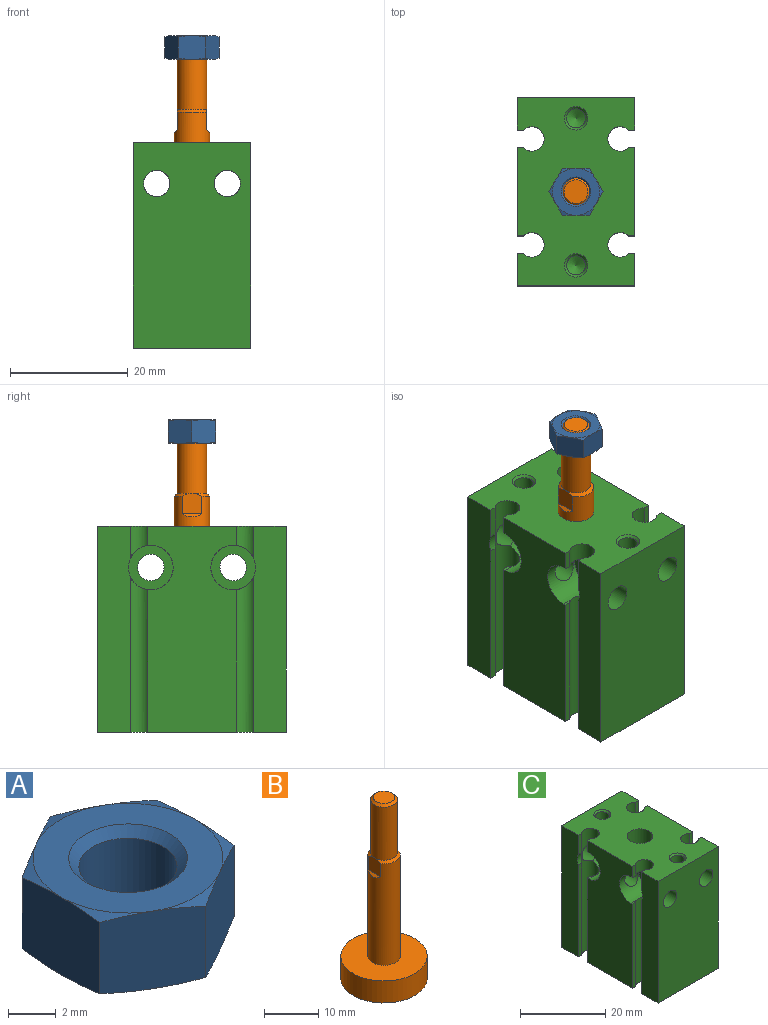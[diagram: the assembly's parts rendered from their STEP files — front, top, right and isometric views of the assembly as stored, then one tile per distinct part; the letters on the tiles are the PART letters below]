
ASSEMBLY  parts=3 mates=2
PART A: 23 faces, bbox 9.6x9.6x4.3 mm
  f0: cone r=4mm half-angle=75deg, axis (0,0,1), area 1.4mm2, adj f16,f17,f22
  f1: cone r=4mm half-angle=75deg, axis (0,0,1), area 1.4mm2, adj f16,f17,f18
  f2: cone r=4mm half-angle=75deg, axis (0,0,1), area 1.4mm2, adj f16,f18,f19
  f3: cone r=4mm half-angle=75deg, axis (0,0,1), area 1.4mm2, adj f16,f19,f20
  f4: cone r=4mm half-angle=75deg, axis (0,0,1), area 1.4mm2, adj f16,f20,f21
  f5: cone r=4mm half-angle=75deg, axis (0,0,1), area 1.4mm2, adj f16,f21,f22
  f6: cone r=7.36mm half-angle=75deg, axis (0,0,-1), area 1.4mm2, adj f12,f19,f20
  f7: cone r=7.36mm half-angle=75deg, axis (0,0,-1), area 1.4mm2, adj f12,f18,f19
  f8: cone r=7.36mm half-angle=75deg, axis (0,0,-1), area 1.4mm2, adj f12,f17,f18
  f9: cone r=7.36mm half-angle=75deg, axis (0,0,-1), area 1.4mm2, adj f12,f20,f21
  f10: cone r=7.36mm half-angle=75deg, axis (0,0,-1), area 1.4mm2, adj f12,f17,f22
  f11: cone r=7.36mm half-angle=75deg, axis (0,0,-1), area 1.4mm2, adj f12,f21,f22
  f12: plane 8x8mm, normal (0,0,1), area 30.6mm2, adj f6,f7,f8,f9,f10,f11,f13
  f13: cone r=2.5mm half-angle=45deg, axis (0,0,1), area 8.8mm2, adj f12,f14
  f14: cylinder r=2.07mm len=4.13mm, axis (0,0,-1), area 40.7mm2, adj f13,f15
  f15: cone r=2.07mm half-angle=45deg, axis (0,0,-1), area 8.8mm2, adj f14,f16
  f16: plane 8x8mm, normal (0,0,-1), area 30.6mm2, adj f0,f1,f2,f3,f4,f5,f15
  f17: plane 4.97x4.35mm, normal (-1,0,0), area 17.9mm2, adj f0,f1,f8,f10,f18,f22
  f18: plane 4.34x4.34mm, normal (-0.5,0.87,0), area 17.9mm2, adj f1,f2,f7,f8,f17,f19
  f19: plane 4.34x4.34mm, normal (0.5,0.87,0), area 17.9mm2, adj f2,f3,f6,f7,f18,f20
  f20: plane 4.97x4.35mm, normal (1,0,0), area 17.9mm2, adj f3,f4,f6,f9,f19,f21
  f21: plane 4.34x4.34mm, normal (0.5,-0.87,0), area 17.9mm2, adj f4,f5,f9,f11,f20,f22
  f22: plane 4.34x4.34mm, normal (-0.5,-0.87,0), area 17.9mm2, adj f0,f5,f10,f11,f17,f21
PART B: 13 faces, bbox 16x16x41 mm
  f0: cone r=2.5mm half-angle=45deg, axis (0,0,-1), area 4.5mm2, adj f2,f5,f9,f12
  f1: cone r=2.5mm half-angle=45deg, axis (0,0,-1), area 4.5mm2, adj f2,f5,f9,f12
  f2: cylinder r=3mm len=23mm, axis (0,0,-1), area 410.1mm2, adj f0,f1,f6,f9,f10,f11,f12
  f3: plane 4.02x4.02mm, normal (0,0,1), area 12.7mm2, adj f4
  f4: cone r=2.01mm half-angle=45deg, axis (0,0,-1), area 9.8mm2, adj f3,f5
  f5: cylinder r=2.5mm len=12.01mm, axis (0,0,-1), area 188.6mm2, adj f0,f1,f4
  f6: plane 16x16mm, normal (0,0,1), area 172.8mm2, adj f2,f7
  f7: cylinder r=8mm len=16mm, axis (0,0,-1), area 251.3mm2, adj f6,f8
  f8: plane 16x16mm, normal (0,0,-1), area 201.1mm2, adj f7
  f9: plane 3.5x3.32mm, normal (-1,0,0), area 11mm2, adj f0,f1,f2,f10
  f10: plane 3.32x0.5mm, normal (-0.71,0,0.71), area 1.6mm2, adj f2,f9
  f11: plane 3.32x0.5mm, normal (0.71,0,0.71), area 1.6mm2, adj f2,f12
  f12: plane 3.5x3.32mm, normal (1,0,0), area 11mm2, adj f0,f1,f2,f11
PART C: 76 faces, bbox 20x32x35 mm
  f0: cylinder r=2.25mm len=7.88mm, axis (0,-1,0), area 100.6mm2, adj f45,f54
  f1: cylinder r=2.25mm len=5.92mm, axis (0,-1,0), area 74.7mm2, adj f5,f28,f54
  f2: cylinder r=2.25mm len=7.88mm, axis (0,-1,0), area 100.6mm2, adj f40,f50
  f3: cylinder r=2.25mm len=5.92mm, axis (0,-1,0), area 74.7mm2, adj f4,f28,f50
  f4: cylinder r=2.1mm len=35mm, axis (0,0,1), area 290mm2, adj f3,f10,f11,f12,f13,f34,f35,f49
  f5: cylinder r=2.1mm len=35mm, axis (0,0,1), area 290mm2, adj f1,f6,f7,f8,f9,f34,f35,f54
  f6: plane 24.23x1.03mm, normal (0,-1,0), area 25mm2, adj f5,f26,f34,f55
  f7: plane 3.23x1.03mm, normal (0,-1,0), area 3.3mm2, adj f5,f26,f35,f54
  f8: plane 5.52x1.03mm, normal (0,1,0), area 5.7mm2, adj f5,f27,f35,f57
  f9: plane 26.52x1.03mm, normal (0,1,0), area 27.3mm2, adj f5,f27,f34,f57
  f10: plane 5.52x1.03mm, normal (0,1,0), area 5.7mm2, adj f4,f29,f35,f56
  f11: plane 26.52x1.03mm, normal (0,1,0), area 27.3mm2, adj f4,f29,f34,f56
  f12: plane 24.23x1.03mm, normal (0,-1,0), area 25mm2, adj f4,f30,f34,f49
  f13: plane 3.23x1.03mm, normal (0,-1,0), area 3.3mm2, adj f4,f30,f35,f50
  f14: cylinder r=2.1mm len=35mm, axis (0,0,1), area 290mm2, adj f16,f17,f18,f19,f25,f34,f35,f40
  f15: cylinder r=2.1mm len=35mm, axis (0,0,1), area 290mm2, adj f20,f21,f22,f23,f24,f34,f35,f45
  f16: plane 3.23x1.03mm, normal (0,1,0), area 3.3mm2, adj f14,f30,f35,f40
  f17: plane 24.23x1.03mm, normal (0,1,0), area 25mm2, adj f14,f30,f34,f41
  f18: plane 26.52x1.03mm, normal (0,-1,0), area 27.3mm2, adj f14,f31,f34,f48
  f19: plane 5.52x1.03mm, normal (0,-1,0), area 5.7mm2, adj f14,f31,f35,f48
  f20: plane 26.52x1.03mm, normal (0,-1,0), area 27.3mm2, adj f15,f33,f34,f47
  f21: plane 5.52x1.03mm, normal (0,-1,0), area 5.7mm2, adj f15,f33,f35,f47
  f22: plane 3.23x1.03mm, normal (0,1,0), area 3.3mm2, adj f15,f26,f35,f45
  f23: plane 24.23x1.03mm, normal (0,1,0), area 25mm2, adj f15,f26,f34,f46
  f24: cylinder r=2.25mm len=5.92mm, axis (0,-1,0), area 74.7mm2, adj f15,f32,f45
  f25: cylinder r=2.25mm len=5.92mm, axis (0,-1,0), area 74.7mm2, adj f14,f32,f40
  f26: plane 35x15mm, normal (-1,0,0), area 472.1mm2, adj f6,f7,f22,f23,f34,f35,f45,f46
  f27: plane 35x5.5mm, normal (-1,0,0), area 191.9mm2, adj f8,f9,f28,f34,f35,f57
  f28: plane 35x20mm, normal (0,-1,0), area 668.2mm2, adj f1,f3,f27,f29,f34,f35
  f29: plane 35x5.5mm, normal (1,0,0), area 191.9mm2, adj f10,f11,f28,f34,f35,f56
  f30: plane 35x15mm, normal (1,0,0), area 472.1mm2, adj f12,f13,f16,f17,f34,f35,f40,f41
  f31: plane 35x5.5mm, normal (1,0,0), area 191.9mm2, adj f18,f19,f32,f34,f35,f48
  f32: plane 35x20mm, normal (0,1,0), area 628.9mm2, adj f24,f25,f31,f33,f34,f35,f70,f73
  f33: plane 35x5.5mm, normal (-1,0,0), area 191.9mm2, adj f20,f21,f32,f34,f35,f47
  f34: plane 32x20mm, normal (0,0,-1), area 552.3mm2, adj f4,f5,f6,f9,f11,f12,f14,f15
  f35: plane 32x20mm, normal (0,0,1), area 524mm2, adj f4,f5,f7,f8,f10,f13,f14,f15
  f36: cylinder r=3mm len=15mm, axis (0,0,-1), area 282.7mm2, adj f35,f37
  f37: plane 16x16mm, normal (0,0,-1), area 172.8mm2, adj f36,f38
  f38: cylinder r=8mm len=16mm, axis (0,0,-1), area 502.7mm2, adj f37,f39
  f39: plane 16x16mm, normal (0,0,1), area 201.1mm2, adj f38
  f40: cylinder r=3.8mm len=7.6mm, axis (1,0,0), area 80.5mm2, adj f2,f14,f16,f25,f30,f41,f42
  f41: cylinder r=3.8mm len=1.86mm, axis (1,0,0), area 0.7mm2, adj f14,f17,f30,f40
  f42: plane 7.6x7.6mm, normal (1,0,0), area 29.5mm2, adj f40,f43
  f43: cylinder r=2.25mm len=7mm, axis (1,0,0), area 99mm2, adj f42,f44
  f44: plane 7.6x7.6mm, normal (-1,0,0), area 29.5mm2, adj f43,f45
  f45: cylinder r=3.8mm len=7.6mm, axis (1,0,0), area 80.5mm2, adj f0,f15,f22,f24,f26,f44,f46
  f46: cylinder r=3.8mm len=1.86mm, axis (1,0,0), area 0.7mm2, adj f15,f23,f26,f45
  f47: cylinder r=3.8mm len=2.96mm, axis (1,0,0), area 3.9mm2, adj f15,f20,f21,f33
  f48: cylinder r=3.8mm len=2.96mm, axis (1,0,0), area 3.9mm2, adj f14,f18,f19,f31
  f49: cylinder r=3.8mm len=1.86mm, axis (1,0,0), area 0.7mm2, adj f4,f12,f30,f50
  f50: cylinder r=3.8mm len=7.6mm, axis (1,0,0), area 80.5mm2, adj f2,f3,f4,f13,f30,f49,f51
  f51: plane 7.6x7.6mm, normal (1,0,0), area 29.5mm2, adj f50,f52
  f52: cylinder r=2.25mm len=7mm, axis (1,0,0), area 99mm2, adj f51,f53
  f53: plane 7.6x7.6mm, normal (-1,0,0), area 29.5mm2, adj f52,f54
  f54: cylinder r=3.8mm len=7.6mm, axis (1,0,0), area 80.5mm2, adj f0,f1,f5,f7,f26,f53,f55
  f55: cylinder r=3.8mm len=1.86mm, axis (1,0,0), area 0.7mm2, adj f5,f6,f26,f54
  f56: cylinder r=3.8mm len=2.96mm, axis (1,0,0), area 3.9mm2, adj f4,f10,f11,f29
  f57: cylinder r=3.8mm len=2.96mm, axis (1,0,0), area 3.9mm2, adj f5,f8,f9,f27
  f58: cone r=2mm half-angle=45deg, axis (0,0,1), area 6.1mm2, adj f35,f59
  f59: cylinder r=1.62mm len=5.62mm, axis (0,0,-1), area 57.3mm2, adj f58,f60
  f60: cone r=1.62mm half-angle=60deg, axis (0,0,1), area 9.5mm2, adj f59
  f61: cone r=2mm half-angle=45deg, axis (0,0,1), area 6.1mm2, adj f35,f62
  f62: cylinder r=1.62mm len=5.62mm, axis (0,0,-1), area 57.3mm2, adj f61,f63
  f63: cone r=1.62mm half-angle=60deg, axis (0,0,1), area 9.5mm2, adj f62
  f64: cone r=0mm half-angle=60deg, axis (0,0,-1), area 9.5mm2, adj f65
  f65: cylinder r=1.62mm len=5.62mm, axis (0,0,-1), area 57.3mm2, adj f64,f66
  f66: cone r=1.62mm half-angle=45deg, axis (0,0,-1), area 6.1mm2, adj f34,f65
  f67: cone r=0mm half-angle=60deg, axis (0,0,-1), area 9.5mm2, adj f68
  f68: cylinder r=1.62mm len=5.62mm, axis (0,0,-1), area 57.3mm2, adj f67,f69
  f69: cone r=1.62mm half-angle=45deg, axis (0,0,-1), area 6.1mm2, adj f34,f68
  f70: cone r=2.5mm half-angle=45deg, axis (0,1,0), area 8.8mm2, adj f32,f71
  f71: cylinder r=2.07mm len=4.57mm, axis (0,-1,0), area 59.3mm2, adj f70,f72
  f72: cone r=2.07mm half-angle=60deg, axis (0,1,0), area 15.5mm2, adj f71
  f73: cone r=2.5mm half-angle=45deg, axis (0,1,0), area 8.8mm2, adj f32,f74
  f74: cylinder r=2.07mm len=4.57mm, axis (0,-1,0), area 59.3mm2, adj f73,f75
  f75: cone r=2.07mm half-angle=60deg, axis (0,1,0), area 15.5mm2, adj f74
PLACE A rot(axis=(0,0,-1),90deg) t=(-38.94,-7.27,26.02)mm
PLACE B rot(axis=(0,0,-1),0deg) t=(-38.94,-7.27,10.02)mm
PLACE C t=(-38.94,-7.27,7.89)mm
MATE cylindrical B.f0 <-> A.f0  axis (0,0,1) through (-38.94,-7.27,26.02)mm
MATE cylindrical C.f36 <-> B.f0  axis (0,0,1) through (-38.94,-7.27,7.89)mm
